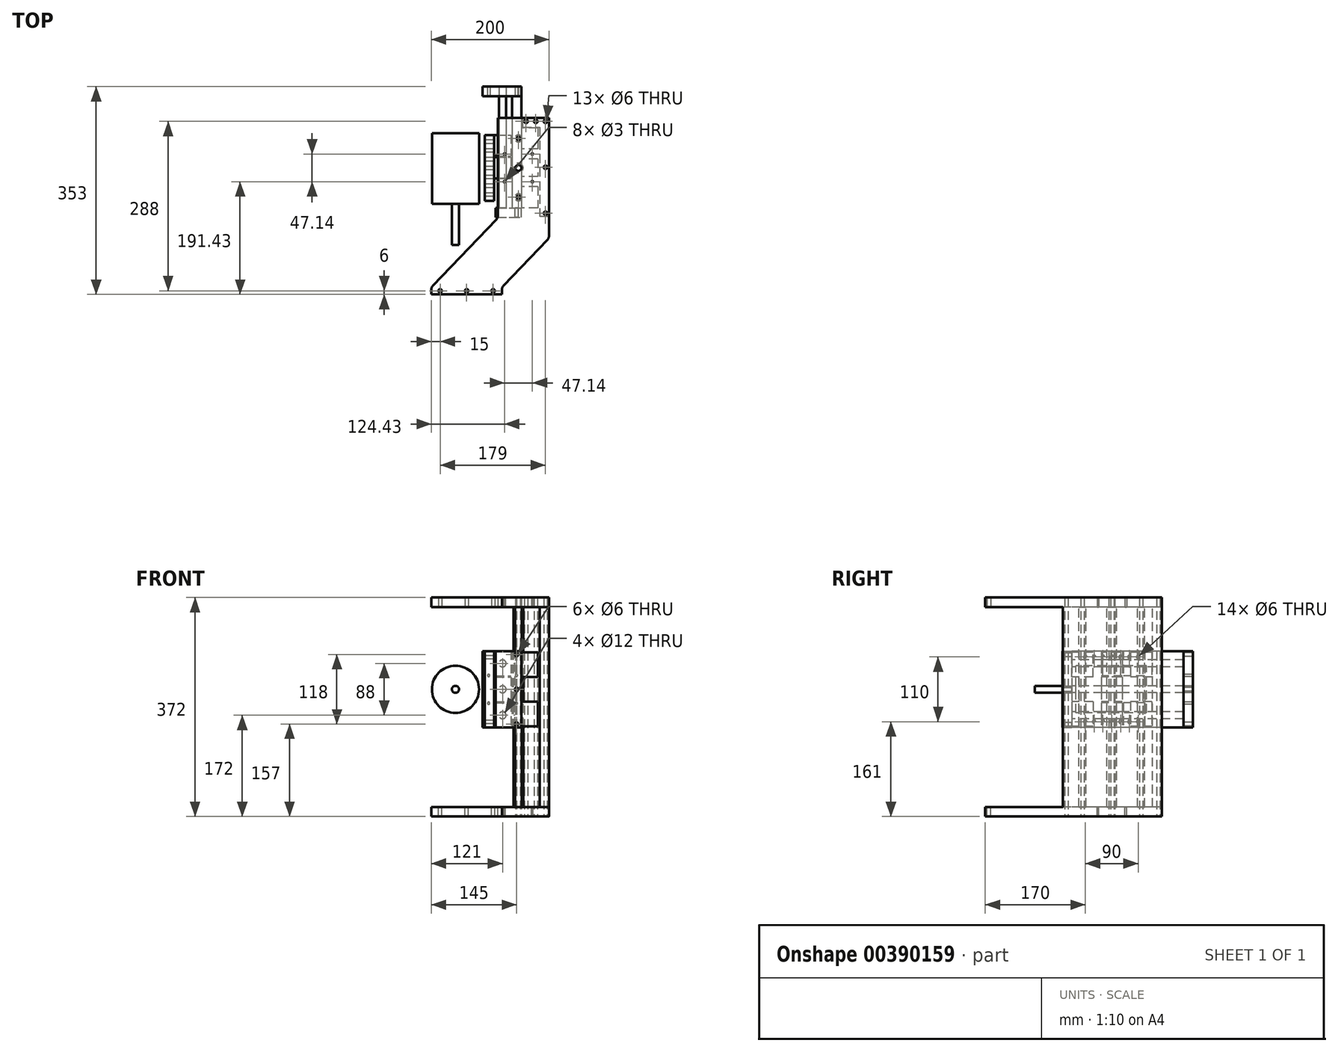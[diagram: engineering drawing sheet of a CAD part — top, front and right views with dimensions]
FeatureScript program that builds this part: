
annotation { "Feature Type Name" : "Feature", "Feature Type Description" : "" }
export const myFeature = defineFeature(function(context is Context, id is Id, definition is map)
    precondition{}
    {
        {
            var Q0;
            Q0=qCreatedBy(makeId("Top.planeOp"),FACE);
            var sketch = newSketch(context, id + "F0", { "sketchPlane" : qUnion([Q0])});
            skLineSegment(sketch, "E0", {"start": v(0, 0) * mm, "end": v(120, 0) * mm});
            skLineSegment(sketch, "E1", {"start": v(122.78, 14.9) * mm, "end": v(197.22, 92.64) * mm});
            skLineSegment(sketch, "E2", {"start": v(200, 99.56) * mm, "end": v(200, 300) * mm});
            skLineSegment(sketch, "E3", {"start": v(200, 300) * mm, "end": v(113, 300) * mm});
            skLineSegment(sketch, "E4", {"start": v(113, 300) * mm, "end": v(113, 134.02) * mm});
            skLineSegment(sketch, "E5", {"start": v(110.22, 127.1) * mm, "end": v(2.78, 14.9) * mm});
            skLineSegment(sketch, "E6.bottom", {"start": v(113, 300) * mm, "end": v(60, 300) * mm, "construction": true});
            skLineSegment(sketch, "E6.top", {"start": v(113, 240) * mm, "end": v(60, 240) * mm, "construction": true});
            skLineSegment(sketch, "E6.left", {"start": v(113, 300) * mm, "end": v(113, 240) * mm, "construction": true});
            skLineSegment(sketch, "E6.right", {"start": v(60, 300) * mm, "end": v(60, 240) * mm, "construction": true});
            skPoint(sketch, "E7", {"position": v(60, 0) * mm});
            skLineSegment(sketch, "E8", {"start": v(0, 0) * mm, "end": v(0, 7.98) * mm});
            skLineSegment(sketch, "E9", {"start": v(120, 0) * mm, "end": v(120, 7.98) * mm});
            skCircle(sketch, "E10", {"center": v(15, 6) * mm, "radius": 3 * mm});
            skCircle(sketch, "E11", {"center": v(105, 6) * mm, "radius": 3 * mm});
            skCircle(sketch, "E12", {"center": v(148, 165) * mm, "radius": 3 * mm});
            skCircle(sketch, "E13", {"center": v(148, 265) * mm, "radius": 3 * mm});
            skPoint(sketch, "E14", {"position": v(128, 300) * mm});
            skCircle(sketch, "E15", {"center": v(148, 215) * mm, "radius": 5 * mm});
            skLineSegment(sketch, "E16", {"start": v(148, 265) * mm, "end": v(148, 165) * mm, "construction": true});
            skCircle(sketch, "E17", {"center": v(194, 294) * mm, "radius": 3 * mm});
            skCircle(sketch, "E18", {"center": v(194, 216) * mm, "radius": 3 * mm});
            skCircle(sketch, "E19", {"center": v(194, 138) * mm, "radius": 3 * mm});
            skLineSegment(sketch, "E20", {"start": v(194, 138) * mm, "end": v(194, 294) * mm, "construction": true});
            skCircle(sketch, "E21", {"center": v(161, 294) * mm, "radius": 3 * mm});
            skPoint(sketch, "E22.visualSharp", {"position": v(0, 12) * mm});
            skArc(sketch, "E22.filletArc", {"start": v(2.78, 14.9) * mm, "mid": v(0.72, 11.71) * mm, "end": v(0, 7.98) * mm});
            skPoint(sketch, "E23.visualSharp", {"position": v(113, 130) * mm});
            skArc(sketch, "E23.filletArc", {"start": v(110.22, 127.1) * mm, "mid": v(112.28, 130.29) * mm, "end": v(113, 134.02) * mm});
            skArc(sketch, "E24.filletArc", {"start": v(197.22, 92.64) * mm, "mid": v(199.28, 95.83) * mm, "end": v(200, 99.56) * mm});
            skPoint(sketch, "E25.visualSharp", {"position": v(120, 12) * mm});
            skArc(sketch, "E25.filletArc", {"start": v(122.78, 14.9) * mm, "mid": v(120.72, 11.71) * mm, "end": v(120, 7.98) * mm});
            skCircle(sketch, "E26", {"center": v(60, 6) * mm, "radius": 3 * mm});
            skPoint(sketch, "E27", {"position": v(156.5, 300) * mm});
            skCircle(sketch, "E28", {"center": v(177.5, 294) * mm, "radius": 3 * mm});
            skCircle(sketch, "E29", {"center": v(148, 265) * mm, "radius": 6 * mm});
            skCircle(sketch, "E30", {"center": v(148, 165) * mm, "radius": 6 * mm});
            skCircle(sketch, "E31", {"center": v(148, 215) * mm, "radius": 8 * mm});
            skLineSegment(sketch, "E32.bottom", {"start": v(200, 300) * mm, "end": v(184, 300) * mm});
            skLineSegment(sketch, "E32.top", {"start": v(200, 132) * mm, "end": v(184, 132) * mm});
            skLineSegment(sketch, "E32.left", {"start": v(200, 300) * mm, "end": v(200, 132) * mm});
            skLineSegment(sketch, "E32.right", {"start": v(184, 300) * mm, "end": v(184, 132) * mm});
            skLineSegment(sketch, "E33.bottom", {"start": v(113, 300) * mm, "end": v(200, 300) * mm});
            skLineSegment(sketch, "E34", {"start": v(113, 284) * mm, "end": v(200, 284) * mm});
            skLineSegment(sketch, "E35", {"start": v(155, 300) * mm, "end": v(155, 284) * mm});
            skLineSegment(sketch, "E36", {"start": v(161, 294) * mm, "end": v(194, 294) * mm, "construction": true});
            skCircle(sketch, "E37", {"center": v(171.57, 238.57) * mm, "radius": 1.5 * mm});
            skCircle(sketch, "E38", {"center": v(124.43, 191.43) * mm, "radius": 1.5 * mm});
            skCircle(sketch, "E39", {"center": v(171.57, 191.43) * mm, "radius": 1.5 * mm});
            skLineSegment(sketch, "E40", {"start": v(171.57, 191.43) * mm, "end": v(171.57, 238.57) * mm, "construction": true});
            skLineSegment(sketch, "E41", {"start": v(124.43, 191.43) * mm, "end": v(171.57, 191.43) * mm, "construction": true});
            skPoint(sketch, "E42", {"position": v(171.57, 215) * mm});
            skPoint(sketch, "E43", {"position": v(148, 191.43) * mm});
            skCircle(sketch, "E44", {"center": v(124.43, 238.57) * mm, "radius": 1.5 * mm});
            skSolve(sketch);
        }
        {
            var Q0;
            Q0=makeQuery(id+"F0.imprint","IMPRINT",FACE,{"disambiguationData":[TD([[makeQuery(id+"F0.imprint","IMPRINT",EDGE,{"derivedFrom":sQuery(id+"F0.wireOp",EDGE,"E0")}),1.0]])]});
            var Q1;
            Q1=makeQuery(id+"F0.imprint","IMPRINT",FACE,{"disambiguationData":[TD([[makeQuery(id+"F0.imprint","IMPRINT",EDGE,{"derivedFrom":sQuery(id+"F0.wireOp",EDGE,"E13")}),-1.0]])]});
            var Q2;
            Q2=makeQuery(id+"F0.imprint","IMPRINT",FACE,{"disambiguationData":[TD([[makeQuery(id+"F0.imprint","IMPRINT",EDGE,{"derivedFrom":sQuery(id+"F0.wireOp",EDGE,"E15")}),-1.0]])]});
            var Q3;
            Q3=makeQuery(id+"F0.imprint","IMPRINT",FACE,{"disambiguationData":[TD([[makeQuery(id+"F0.imprint","IMPRINT",EDGE,{"derivedFrom":sQuery(id+"F0.wireOp",EDGE,"E12")}),-1.0]])]});
            var Q4;
            Q4=makeQuery(id+"F0.imprint","IMPRINT",FACE,{"disambiguationData":[TD([[makeQuery(id+"F0.imprint","IMPRINT",EDGE,{"derivedFrom":sQuery(id+"F0.wireOp",EDGE,"E17")}),-1.0]])]});
            var Q5;
            Q5=makeQuery(id+"F0.imprint","IMPRINT",FACE,{"disambiguationData":[TD([[makeQuery(id+"F0.imprint","IMPRINT",EDGE,{"derivedFrom":sQuery(id+"F0.wireOp",EDGE,"E21")}),-1.0]])]});
            var Q6;
            Q6=makeQuery(id+"F0.imprint","IMPRINT",FACE,{"disambiguationData":[TD([[makeQuery(id+"F0.imprint","IMPRINT",EDGE,{"derivedFrom":sQuery(id+"F0.wireOp",EDGE,"E18")}),-1.0]])]});
            var Q7;
            Q7=makeQuery(id+"F0.imprint","IMPRINT",FACE,{"disambiguationData":[TD([[makeQuery(id+"F0.imprint","IMPRINT",EDGE,{"derivedFrom":sQuery(id+"F0.wireOp",EDGE,"E28")}),-1.0]])]});
            var Q8;
            {var subQ5=sQuery(id+"F0.wireOp",EDGE,"E35");Q8=makeQuery(id+"F0.imprint","IMPRINT",FACE,{"disambiguationData":[TD([[makeQuery(id+"F0.imprint","IMPRINT",EDGE,{"derivedFrom":subQ5}),-1.0]])]});}
            extrude(context, id + "F1", {"entities" : qUnion([Q0, Q1, Q2, Q3, Q4, Q5, Q6, Q7, Q8]), "depth" : 16 * mm});
        }
        {
            var Q0;
            Q0=qCreatedBy(makeId("Top.planeOp"),FACE);
            cPlane(context, id + "F2", {"entities" : qUnion([Q0]), "cplaneType" : CPlaneType.OFFSET, "offset" : 170 * mm, "oppositeDirection" : true, "width" : 150 * mm, "height" : 150 * mm});
        }
        {
            var Q0;
            Q0=makeQuery(id+"F1.opExtrude","SWEPT_BODY",BODY,{"disambiguationData":[OSD([sQuery(id+"F0.wireOp",EDGE,"E0"),sQuery(id+"F0.wireOp",EDGE,"E1"),sQuery(id+"F0.wireOp",EDGE,"E2"),sQuery(id+"F0.wireOp",EDGE,"E3"),sQuery(id+"F0.wireOp",EDGE,"E4"),sQuery(id+"F0.wireOp",EDGE,"E5"),sQuery(id+"F0.wireOp",EDGE,"E8"),sQuery(id+"F0.wireOp",EDGE,"E9"),sQuery(id+"F0.wireOp",EDGE,"E10"),sQuery(id+"F0.wireOp",EDGE,"E11"),sQuery(id+"F0.wireOp",EDGE,"E12"),sQuery(id+"F0.wireOp",EDGE,"E13"),sQuery(id+"F0.wireOp",EDGE,"E15"),sQuery(id+"F0.wireOp",EDGE,"E17"),sQuery(id+"F0.wireOp",EDGE,"E18"),sQuery(id+"F0.wireOp",EDGE,"E19"),sQuery(id+"F0.wireOp",EDGE,"E21"),sQuery(id+"F0.wireOp",EDGE,"E22.filletArc"),sQuery(id+"F0.wireOp",EDGE,"E23.filletArc"),sQuery(id+"F0.wireOp",EDGE,"E24.filletArc"),sQuery(id+"F0.wireOp",EDGE,"E25.filletArc"),sQuery(id+"F0.wireOp",EDGE,"E26"),sQuery(id+"F0.wireOp",EDGE,"E28")])]});
            var Q1;
            Q1=qCreatedBy(id+"F2.planeOp",FACE);
            mirror(context, id + "F3", {"entities" : qUnion([Q0]), "mirrorPlane" : qUnion([Q1])});
        }
        {
            var Q0;
            Q0=makeQuery(id+"F0.imprint","IMPRINT",FACE,{"disambiguationData":[TD([[makeQuery(id+"F0.imprint","IMPRINT",EDGE,{"derivedFrom":sQuery(id+"F0.wireOp",EDGE,"E13")}),-1.0]])]});
            var Q1;
            Q1=makeQuery(id+"F0.imprint","IMPRINT",FACE,{"disambiguationData":[TD([[makeQuery(id+"F0.imprint","IMPRINT",EDGE,{"derivedFrom":sQuery(id+"F0.wireOp",EDGE,"E12")}),-1.0]])]});
            var Q2;
            Q2=makeQuery(id+"F0.imprint","IMPRINT",FACE,{"disambiguationData":[TD([[makeQuery(id+"F0.imprint","IMPRINT",EDGE,{"derivedFrom":sQuery(id+"F0.wireOp",EDGE,"E15")}),-1.0]])]});
            var Q3;
            Q3=qCreatedBy(id+"F2.planeOp",FACE);
            extrude(context, id + "F4", {"entities" : qUnion([Q0, Q1, Q2]), "endBound" : BoundingType.UP_TO_SURFACE, "oppositeDirection" : true, "endBoundEntityFace" : qUnion([Q3]), "depth" : 100 * mm});
        }
        {
            var Q0;
            Q0=makeQuery(id+"F4.opExtrude","SWEPT_BODY",BODY,{"disambiguationData":[OSD([sQuery(id+"F0.wireOp",EDGE,"E12"),sQuery(id+"F0.wireOp",EDGE,"E30")])]});
            var Q1;
            Q1=makeQuery(id+"F4.opExtrude","SWEPT_BODY",BODY,{"disambiguationData":[OSD([sQuery(id+"F0.wireOp",EDGE,"E15"),sQuery(id+"F0.wireOp",EDGE,"E31")])]});
            var Q2;
            Q2=makeQuery(id+"F4.opExtrude","SWEPT_BODY",BODY,{"disambiguationData":[OSD([sQuery(id+"F0.wireOp",EDGE,"E13"),sQuery(id+"F0.wireOp",EDGE,"E29")])]});
            var Q3;
            Q3=qCreatedBy(id+"F2.planeOp",FACE);
            mirror(context, id + "F5", {"operationType" : NewBodyOperationType.ADD, "entities" : qUnion([Q0, Q1, Q2]), "mirrorPlane" : qUnion([Q3])});
        }
        {
            var Q0;
            Q0=makeQuery(id+"F1.opExtrude","SWEPT_FACE",FACE,{"disambiguationData":[OSD([sQuery(id+"F0.wireOp",EDGE,"E4")])]});
            cPlane(context, id + "F6", {"entities" : qUnion([Q0]), "cplaneType" : CPlaneType.OFFSET, "offset" : 40 * mm, "oppositeDirection" : true, "width" : 150 * mm, "height" : 150 * mm});
        }
        {
            var Q0;
            Q0=qCreatedBy(id+"F6.planeOp",FACE);
            var sketch = newSketch(context, id + "F7", { "sketchPlane" : qUnion([Q0])});
            skLineSegment(sketch, "E45.bottom", {"start": v(-283, -77) * mm, "end": v(-247, -77) * mm});
            skLineSegment(sketch, "E45.top", {"start": v(-283, -119) * mm, "end": v(-247, -119) * mm});
            skLineSegment(sketch, "E45.left", {"start": v(-283, -77) * mm, "end": v(-283, -119) * mm});
            skLineSegment(sketch, "E45.right", {"start": v(-247, -77) * mm, "end": v(-247, -119) * mm});
            skPoint(sketch, "E46", {"position": v(-265, -77) * mm});
            skLineSegment(sketch, "E47.bottom", {"start": v(-183, -119) * mm, "end": v(-147, -119) * mm});
            skLineSegment(sketch, "E47.top", {"start": v(-183, -77) * mm, "end": v(-147, -77) * mm});
            skLineSegment(sketch, "E47.left", {"start": v(-183, -119) * mm, "end": v(-183, -77) * mm});
            skLineSegment(sketch, "E47.right", {"start": v(-147, -119) * mm, "end": v(-147, -77) * mm});
            skPoint(sketch, "E48", {"position": v(-165, -77) * mm});
            skLineSegment(sketch, "E49.bottom", {"start": v(-230, -119) * mm, "end": v(-200, -119) * mm});
            skLineSegment(sketch, "E49.top", {"start": v(-230, -77) * mm, "end": v(-200, -77) * mm});
            skLineSegment(sketch, "E49.left", {"start": v(-230, -119) * mm, "end": v(-230, -77) * mm});
            skLineSegment(sketch, "E49.right", {"start": v(-200, -119) * mm, "end": v(-200, -77) * mm});
            skPoint(sketch, "E50", {"position": v(-215, -77) * mm});
            skLineSegment(sketch, "E51.bottom", {"start": v(-337, -75) * mm, "end": v(-147, -75) * mm});
            skLineSegment(sketch, "E51.top", {"start": v(-337, -205) * mm, "end": v(-147, -205) * mm});
            skLineSegment(sketch, "E51.left", {"start": v(-337, -75) * mm, "end": v(-337, -205) * mm});
            skLineSegment(sketch, "E51.right", {"start": v(-147, -75) * mm, "end": v(-147, -205) * mm});
            skPoint(sketch, "E52", {"position": v(-200, -98) * mm});
            skPoint(sketch, "E53.oppositeSnap0", {"position": v(-247, -98) * mm});
            skLineSegment(sketch, "E53.bottom", {"start": v(-283, -161) * mm, "end": v(-247, -161) * mm});
            skLineSegment(sketch, "E53.top", {"start": v(-283, -203) * mm, "end": v(-247, -203) * mm});
            skLineSegment(sketch, "E53.left", {"start": v(-283, -161) * mm, "end": v(-283, -203) * mm});
            skLineSegment(sketch, "E53.right", {"start": v(-247, -161) * mm, "end": v(-247, -203) * mm});
            skPoint(sketch, "E54.firstSnap0", {"position": v(-230, -98) * mm});
            skPoint(sketch, "E55.firstSnap0", {"position": v(-183, -98) * mm});
            skLineSegment(sketch, "E55.bottom", {"start": v(-183, -161) * mm, "end": v(-147, -161) * mm});
            skLineSegment(sketch, "E55.top", {"start": v(-183, -203) * mm, "end": v(-147, -203) * mm});
            skLineSegment(sketch, "E55.left", {"start": v(-183, -161) * mm, "end": v(-183, -203) * mm});
            skLineSegment(sketch, "E55.right", {"start": v(-147, -161) * mm, "end": v(-147, -203) * mm});
            skLineSegment(sketch, "E56.0", {"start": v(-300, 0) * mm, "end": v(-134.02, 0) * mm, "construction": true});
            skSolve(sketch);
        }
        {
            var Q0;
            Q0=makeQuery(id+"F7.imprint","IMPRINT",FACE,{"disambiguationData":[TD([[makeQuery(id+"F7.imprint","IMPRINT",EDGE,{"derivedFrom":sQuery(id+"F7.wireOp",EDGE,"E45.bottom")}),-1.0]])]});
            var Q1;
            Q1=makeQuery(id+"F7.imprint","IMPRINT",FACE,{"disambiguationData":[TD([[makeQuery(id+"F7.imprint","IMPRINT",EDGE,{"derivedFrom":sQuery(id+"F7.wireOp",EDGE,"E47.bottom")}),1.0]])]});
            var Q2;
            Q2=makeQuery(id+"F7.imprint","IMPRINT",FACE,{"disambiguationData":[TD([[makeQuery(id+"F7.imprint","IMPRINT",EDGE,{"derivedFrom":sQuery(id+"F7.wireOp",EDGE,"E49.bottom")}),1.0]])]});
            var Q3;
            Q3=makeQuery(id+"F7.imprint","IMPRINT",FACE,{"disambiguationData":[TD([[makeQuery(id+"F7.imprint","IMPRINT",EDGE,{"derivedFrom":sQuery(id+"F7.wireOp",EDGE,"E53.bottom")}),-1.0]])]});
            var Q4;
            Q4=makeQuery(id+"F7.imprint","IMPRINT",FACE,{"disambiguationData":[TD([[makeQuery(id+"F7.imprint","IMPRINT",EDGE,{"derivedFrom":sQuery(id+"F7.wireOp",EDGE,"E54.bottom")}),-1.0]])]});
            var Q5;
            Q5=makeQuery(id+"F7.imprint","IMPRINT",FACE,{"disambiguationData":[TD([[makeQuery(id+"F7.imprint","IMPRINT",EDGE,{"derivedFrom":sQuery(id+"F7.wireOp",EDGE,"E55.bottom")}),-1.0]])]});
            extrude(context, id + "F8", {"entities" : qUnion([Q0, Q1, Q2, Q3, Q4, Q5]), "oppositeDirection" : true, "depth" : 28 * mm});
        }
        {
            var Q0;
            Q0=makeQuery(id+"F7.imprint","IMPRINT",FACE,{"disambiguationData":[TD([[makeQuery(id+"F7.imprint","IMPRINT",EDGE,{"derivedFrom":sQuery(id+"F7.wireOp",EDGE,"E45.bottom")}),1.0]])]});
            var Q1;
            Q1=makeQuery(id+"F7.imprint","IMPRINT",FACE,{"disambiguationData":[TD([[makeQuery(id+"F7.imprint","IMPRINT",EDGE,{"derivedFrom":sQuery(id+"F7.wireOp",EDGE,"E47.bottom")}),1.0]])]});
            var Q2;
            Q2=makeQuery(id+"F7.imprint","IMPRINT",FACE,{"disambiguationData":[TD([[makeQuery(id+"F7.imprint","IMPRINT",EDGE,{"derivedFrom":sQuery(id+"F7.wireOp",EDGE,"E49.bottom")}),1.0]])]});
            var Q3;
            Q3=makeQuery(id+"F7.imprint","IMPRINT",FACE,{"disambiguationData":[TD([[makeQuery(id+"F7.imprint","IMPRINT",EDGE,{"derivedFrom":sQuery(id+"F7.wireOp",EDGE,"E45.bottom")}),-1.0]])]});
            var Q4;
            Q4=makeQuery(id+"F7.imprint","IMPRINT",FACE,{"disambiguationData":[TD([[makeQuery(id+"F7.imprint","IMPRINT",EDGE,{"derivedFrom":sQuery(id+"F7.wireOp",EDGE,"E53.bottom")}),-1.0]])]});
            var Q5;
            Q5=makeQuery(id+"F7.imprint","IMPRINT",FACE,{"disambiguationData":[TD([[makeQuery(id+"F7.imprint","IMPRINT",EDGE,{"derivedFrom":sQuery(id+"F7.wireOp",EDGE,"E54.bottom")}),-1.0]])]});
            var Q6;
            Q6=makeQuery(id+"F7.imprint","IMPRINT",FACE,{"disambiguationData":[TD([[makeQuery(id+"F7.imprint","IMPRINT",EDGE,{"derivedFrom":sQuery(id+"F7.wireOp",EDGE,"E55.bottom")}),-1.0]])]});
            extrude(context, id + "F9", {"entities" : qUnion([Q0, Q1, Q2, Q3, Q4, Q5, Q6]), "depth" : 16 * mm});
        }
        {
            var Q0;
            Q0=makeQuery(id+"F9.opExtrude","SWEPT_FACE",FACE,{"disambiguationData":[OSD([sQuery(id+"F7.wireOp",EDGE,"E51.left")])]});
            cPlane(context, id + "F10", {"entities" : qUnion([Q0]), "cplaneType" : CPlaneType.OFFSET, "offset" : 0 * mm, "width" : 150 * mm, "height" : 150 * mm});
        }
        {
            var Q0;
            Q0=qCreatedBy(id+"F10.planeOp",FACE);
            var sketch = newSketch(context, id + "F11", { "sketchPlane" : qUnion([Q0])});
            skLineSegment(sketch, "E57.top", {"start": v(-153, -205) * mm, "end": v(-87, -205) * mm});
            skLineSegment(sketch, "E57.left", {"start": v(-153, -75) * mm, "end": v(-153, -205) * mm});
            skLineSegment(sketch, "E57.right", {"start": v(-87, -75) * mm, "end": v(-87, -205) * mm});
            skLineSegment(sketch, "E58", {"start": v(-137, -75) * mm, "end": v(-137, -205) * mm});
            skPoint(sketch, "E59", {"position": v(-112, -75) * mm});
            skPoint(sketch, "E60", {"position": v(-87, -140) * mm});
            skLineSegment(sketch, "E61", {"start": v(-153, -75) * mm, "end": v(-137, -75) * mm});
            skLineSegment(sketch, "E62", {"start": v(-87, -75) * mm, "end": v(-137, -75) * mm});
            skCircle(sketch, "E63", {"center": v(-145, -81) * mm, "radius": 3 * mm});
            skCircle(sketch, "E64", {"center": v(-145, -140) * mm, "radius": 3 * mm});
            skCircle(sketch, "E65", {"center": v(-145, -199) * mm, "radius": 3 * mm});
            skLineSegment(sketch, "E66", {"start": v(-145, -199) * mm, "end": v(-145, -81) * mm, "construction": true});
            skPoint(sketch, "E67", {"position": v(-145, -75) * mm});
            skPoint(sketch, "E68", {"position": v(-137, -140) * mm});
            skLineSegment(sketch, "E69.0", {"start": v(-137, -205) * mm, "end": v(-153, -205) * mm, "construction": true});
            skLineSegment(sketch, "E70.0", {"start": v(-137, -75) * mm, "end": v(-153, -75) * mm, "construction": true});
            skCircle(sketch, "E71", {"center": v(-121, -140) * mm, "radius": 6 * mm});
            skCircle(sketch, "E72", {"center": v(-144.57, -116.43) * mm, "radius": 2 * mm});
            skCircle(sketch, "E73", {"center": v(-97.43, -116.43) * mm, "radius": 2 * mm});
            skCircle(sketch, "E74", {"center": v(-97.43, -163.57) * mm, "radius": 2 * mm});
            skCircle(sketch, "E75", {"center": v(-144.57, -163.57) * mm, "radius": 2 * mm});
            skLineSegment(sketch, "E76", {"start": v(-144.57, -163.57) * mm, "end": v(-97.43, -163.57) * mm, "construction": true});
            skLineSegment(sketch, "E77", {"start": v(-97.43, -163.57) * mm, "end": v(-97.43, -116.43) * mm, "construction": true});
            skPoint(sketch, "E78", {"position": v(-121, -163.57) * mm});
            skPoint(sketch, "E79", {"position": v(-97.43, -140) * mm});
            skSolve(sketch);
        }
        {
            var Q0;
            {var subQ0=sQuery(id+"F11.wireOp",EDGE,"E57.right");Q0=makeQuery(id+"F11.imprint","IMPRINT",FACE,{"disambiguationData":[TD([[makeQuery(id+"F11.imprint","IMPRINT",EDGE,{"derivedFrom":subQ0}),-1.0]])]});}
            var Q1;
            {var subQ1=sQuery(id+"F11.wireOp",EDGE,"E57.left");Q1=makeQuery(id+"F11.imprint","IMPRINT",FACE,{"disambiguationData":[TD([[makeQuery(id+"F11.imprint","IMPRINT",EDGE,{"derivedFrom":subQ1}),1.0]])]});}
            extrude(context, id + "F12", {"entities" : qUnion([Q0, Q1]), "depth" : 16 * mm});
        }
        {
            var Q0;
            Q0=makeQuery(id+"F9.opExtrude","SWEPT_FACE",FACE,{"disambiguationData":[OSD([sQuery(id+"F7.wireOp",EDGE,"E51.right")])]});
            cPlane(context, id + "F13", {"entities" : qUnion([Q0]), "cplaneType" : CPlaneType.OFFSET, "offset" : 0 * mm, "width" : 150 * mm, "height" : 150 * mm});
        }
        {
            var Q0;
            Q0=qCreatedBy(id+"F13.planeOp",FACE);
            var sketch = newSketch(context, id + "F14", { "sketchPlane" : qUnion([Q0])});
            skLineSegment(sketch, "E80.bottom", {"start": v(109, -75) * mm, "end": v(153, -75) * mm});
            skLineSegment(sketch, "E80.top", {"start": v(109, -205) * mm, "end": v(153, -205) * mm});
            skLineSegment(sketch, "E80.left", {"start": v(109, -75) * mm, "end": v(109, -205) * mm});
            skLineSegment(sketch, "E80.right", {"start": v(153, -75) * mm, "end": v(153, -205) * mm});
            skLineSegment(sketch, "E81", {"start": v(137, -75) * mm, "end": v(137, -205) * mm, "construction": true});
            skCircle(sketch, "E82.0", {"center": v(145, -81) * mm, "radius": 3 * mm});
            skCircle(sketch, "E82.1", {"center": v(145, -199) * mm, "radius": 3 * mm});
            skCircle(sketch, "E82.2", {"center": v(145, -140) * mm, "radius": 3 * mm});
            skLineSegment(sketch, "E83.0", {"start": v(87, -75) * mm, "end": v(153, -75) * mm, "construction": true});
            skSolve(sketch);
        }
        {
            var Q0;
            Q0=makeQuery(id+"F14.imprint","IMPRINT",FACE,{"disambiguationData":[TD([[makeQuery(id+"F14.imprint","IMPRINT",EDGE,{"derivedFrom":sQuery(id+"F14.wireOp",EDGE,"E80.bottom")}),-1.0]])]});
            extrude(context, id + "F15", {"entities" : qUnion([Q0]), "depth" : 16 * mm});
        }
        {
            var Q0;
            Q0=makeQuery(id+"F0.imprint","IMPRINT",FACE,{"disambiguationData":[TD([[makeQuery(id+"F0.imprint","IMPRINT",EDGE,{"derivedFrom":sQuery(id+"F0.wireOp",EDGE,"E18")}),-1.0]])]});
            var Q1;
            Q1=qCreatedBy(id+"F2.planeOp",FACE);
            extrude(context, id + "F16", {"entities" : qUnion([Q0]), "endBound" : BoundingType.UP_TO_SURFACE, "oppositeDirection" : true, "endBoundEntityFace" : qUnion([Q1]), "depth" : 100 * mm});
        }
        {
            var Q0;
            Q0=makeQuery(id+"F16.opExtrude","SWEPT_BODY",BODY,{"disambiguationData":[OSD([sQuery(id+"F0.wireOp",EDGE,"E17"),sQuery(id+"F0.wireOp",EDGE,"E18"),sQuery(id+"F0.wireOp",EDGE,"E19"),sQuery(id+"F0.wireOp",EDGE,"E24.filletArc"),sQuery(id+"F0.wireOp",EDGE,"E32.bottom"),sQuery(id+"F0.wireOp",EDGE,"E32.top"),sQuery(id+"F0.wireOp",EDGE,"E32.left"),sQuery(id+"F0.wireOp",EDGE,"E32.right")])]});
            var Q1;
            Q1=qCreatedBy(id+"F2.planeOp",FACE);
            mirror(context, id + "F17", {"operationType" : NewBodyOperationType.ADD, "entities" : qUnion([Q0]), "mirrorPlane" : qUnion([Q1])});
        }
        {
            var Q0;
            Q0=makeQuery(id+"F0.imprint","IMPRINT",FACE,{"disambiguationData":[TD([[makeQuery(id+"F0.imprint","IMPRINT",EDGE,{"derivedFrom":sQuery(id+"F0.wireOp",EDGE,"E28")}),-1.0]])]});
            var Q1;
            Q1=makeQuery(id+"F0.imprint","IMPRINT",FACE,{"disambiguationData":[TD([[makeQuery(id+"F0.imprint","IMPRINT",EDGE,{"derivedFrom":sQuery(id+"F0.wireOp",EDGE,"E17")}),-1.0]])]});
            var Q2;
            Q2=qCreatedBy(id+"F2.planeOp",FACE);
            extrude(context, id + "F18", {"entities" : qUnion([Q0, Q1]), "endBound" : BoundingType.UP_TO_SURFACE, "oppositeDirection" : true, "endBoundEntityFace" : qUnion([Q2]), "depth" : 100 * mm});
        }
        {
            var Q0;
            Q0=makeQuery(id+"F18.opExtrude","SWEPT_BODY",BODY,{"disambiguationData":[OSD([sQuery(id+"F0.wireOp",EDGE,"E4"),sQuery(id+"F0.wireOp",EDGE,"E32.right"),sQuery(id+"F0.wireOp",EDGE,"E33.bottom"),sQuery(id+"F0.wireOp",EDGE,"E34")])]});
            var Q1;
            Q1=qCreatedBy(id+"F2.planeOp",FACE);
            mirror(context, id + "F19", {"operationType" : NewBodyOperationType.ADD, "entities" : qUnion([Q0]), "mirrorPlane" : qUnion([Q1])});
        }
        {
            var Q0;
            Q0=makeQuery(id+"F15.opExtrude","CAP_FACE",FACE,{"disambiguationData":[OSD([sQuery(id+"F14.wireOp",EDGE,"E80.bottom"),sQuery(id+"F14.wireOp",EDGE,"E80.top"),sQuery(id+"F14.wireOp",EDGE,"E80.left"),sQuery(id+"F14.wireOp",EDGE,"E80.right")])],"isStart":true});
            cPlane(context, id + "F20", {"entities" : qUnion([Q0]), "cplaneType" : CPlaneType.OFFSET, "offset" : 0 * mm, "width" : 150 * mm, "height" : 150 * mm});
        }
        {
            var Q0;
            Q0=qCreatedBy(id+"F20.planeOp",FACE);
            var sketch = newSketch(context, id + "F21", { "sketchPlane" : qUnion([Q0])});
            skCircle(sketch, "E84", {"center": v(-121, -96) * mm, "radius": 6 * mm});
            skCircle(sketch, "E85", {"center": v(-121, -184) * mm, "radius": 6 * mm});
            skCircle(sketch, "E86", {"center": v(-121, -140) * mm, "radius": 6 * mm});
            skLineSegment(sketch, "E87", {"start": v(-121, -96) * mm, "end": v(-121, -184) * mm, "construction": true});
            skLineSegment(sketch, "E88.0", {"start": v(-109, -75) * mm, "end": v(-109, -205) * mm, "construction": true});
            skSolve(sketch);
        }
        {
            var Q0;
            Q0=makeQuery(id+"F21.imprint","IMPRINT",FACE,{"disambiguationData":[TD([[makeQuery(id+"F21.imprint","IMPRINT",EDGE,{"derivedFrom":sQuery(id+"F21.wireOp",EDGE,"E85")}),1.0]])]});
            var Q1;
            Q1=makeQuery(id+"F21.imprint","IMPRINT",FACE,{"disambiguationData":[TD([[makeQuery(id+"F21.imprint","IMPRINT",EDGE,{"derivedFrom":sQuery(id+"F21.wireOp",EDGE,"E86")}),1.0]])]});
            var Q2;
            Q2=makeQuery(id+"F21.imprint","IMPRINT",FACE,{"disambiguationData":[TD([[makeQuery(id+"F21.imprint","IMPRINT",EDGE,{"derivedFrom":sQuery(id+"F21.wireOp",EDGE,"E84")}),1.0]])]});
            extrude(context, id + "F22", {"entities" : qUnion([Q0, Q1, Q2]), "depth" : 190 * mm});
        }
        {
            var Q0;
            Q0=qCreatedBy(id+"F20.planeOp",FACE);
            cPlane(context, id + "F23", {"entities" : qUnion([Q0]), "cplaneType" : CPlaneType.OFFSET, "offset" : 50 * mm, "width" : 150 * mm, "height" : 150 * mm});
        }
        {
            var Q0;
            Q0=qCreatedBy(id+"F23.planeOp",FACE);
            var sketch = newSketch(context, id + "F24", { "sketchPlane" : qUnion([Q0])});
            skCircle(sketch, "E89.0", {"center": v(-121, -96) * mm, "radius": 6 * mm});
            skCircle(sketch, "E89.1", {"center": v(-121, -140) * mm, "radius": 6 * mm});
            skCircle(sketch, "E89.2", {"center": v(-121, -184) * mm, "radius": 6 * mm});
            skLineSegment(sketch, "E90.bottom", {"start": v(-107, -75) * mm, "end": v(-135, -75) * mm});
            skLineSegment(sketch, "E90.top", {"start": v(-107, -117) * mm, "end": v(-135, -117) * mm});
            skLineSegment(sketch, "E90.left", {"start": v(-107, -75) * mm, "end": v(-107, -117) * mm});
            skLineSegment(sketch, "E90.right", {"start": v(-135, -75) * mm, "end": v(-135, -117) * mm});
            skLineSegment(sketch, "E91.bottom", {"start": v(-107, -163) * mm, "end": v(-135, -163) * mm});
            skLineSegment(sketch, "E91.top", {"start": v(-107, -205) * mm, "end": v(-135, -205) * mm});
            skLineSegment(sketch, "E91.left", {"start": v(-107, -163) * mm, "end": v(-107, -205) * mm});
            skLineSegment(sketch, "E91.right", {"start": v(-135, -163) * mm, "end": v(-135, -205) * mm});
            skLineSegment(sketch, "E92.bottom", {"start": v(-107, -119) * mm, "end": v(-135, -119) * mm});
            skLineSegment(sketch, "E92.top", {"start": v(-107, -161) * mm, "end": v(-135, -161) * mm});
            skLineSegment(sketch, "E92.left", {"start": v(-107, -119) * mm, "end": v(-107, -161) * mm});
            skLineSegment(sketch, "E92.right", {"start": v(-135, -119) * mm, "end": v(-135, -161) * mm});
            skSolve(sketch);
        }
        {
            var Q0;
            Q0=makeQuery(id+"F24.imprint","IMPRINT",FACE,{"disambiguationData":[TD([[makeQuery(id+"F24.imprint","IMPRINT",EDGE,{"derivedFrom":sQuery(id+"F24.wireOp",EDGE,"E89.2")}),-1.0]])]});
            var Q1;
            Q1=makeQuery(id+"F24.imprint","IMPRINT",FACE,{"disambiguationData":[TD([[makeQuery(id+"F24.imprint","IMPRINT",EDGE,{"derivedFrom":sQuery(id+"F24.wireOp",EDGE,"E89.0")}),-1.0]])]});
            extrude(context, id + "F25", {"entities" : qUnion([Q0, Q1]), "depth" : 36 * mm});
        }
        {
            var Q0;
            Q0=makeQuery(id+"F24.imprint","IMPRINT",FACE,{"disambiguationData":[TD([[makeQuery(id+"F24.imprint","IMPRINT",EDGE,{"derivedFrom":sQuery(id+"F24.wireOp",EDGE,"E89.1")}),-1.0]])]});
            extrude(context, id + "F26", {"entities" : qUnion([Q0]), "depth" : 36 * mm});
        }
        {
            var Q0;
            Q0=makeQuery(id+"F25.opExtrude","SWEPT_FACE",FACE,{"disambiguationData":[OSD([sQuery(id+"F24.wireOp",EDGE,"E90.left")])]});
            cPlane(context, id + "F27", {"entities" : qUnion([Q0]), "cplaneType" : CPlaneType.OFFSET, "offset" : 0 * mm, "width" : 150 * mm, "height" : 150 * mm});
        }
        {
            var Q0;
            Q0=qCreatedBy(id+"F27.planeOp",FACE);
            var sketch = newSketch(context, id + "F28", { "sketchPlane" : qUnion([Q0])});
            skLineSegment(sketch, "E93.bottom", {"start": v(-271, -75) * mm, "end": v(-159, -75) * mm});
            skLineSegment(sketch, "E93.top", {"start": v(-271, -205) * mm, "end": v(-159, -205) * mm});
            skLineSegment(sketch, "E93.left", {"start": v(-271, -75) * mm, "end": v(-271, -205) * mm});
            skLineSegment(sketch, "E93.right", {"start": v(-159, -75) * mm, "end": v(-159, -205) * mm});
            skLineSegment(sketch, "E94.0", {"start": v(-233, -75) * mm, "end": v(-197, -75) * mm, "construction": true});
            skPoint(sketch, "E95", {"position": v(-215, -75) * mm});
            skPoint(sketch, "E96", {"position": v(-159, -140) * mm});
            skLineSegment(sketch, "E97.0", {"start": v(-197, -119) * mm, "end": v(-197, -161) * mm, "construction": true});
            skPoint(sketch, "E98", {"position": v(-197, -140) * mm});
            skCircle(sketch, "E99", {"center": v(-215, -85) * mm, "radius": 3 * mm});
            skCircle(sketch, "E100", {"center": v(-215, -195) * mm, "radius": 3 * mm});
            skLineSegment(sketch, "E101", {"start": v(-215, -75) * mm, "end": v(-215, -205) * mm, "construction": true});
            skPoint(sketch, "E102", {"position": v(-215, -140) * mm});
            skCircle(sketch, "E103", {"center": v(-200, -85) * mm, "radius": 3 * mm});
            skCircle(sketch, "E104", {"center": v(-185, -85) * mm, "radius": 3 * mm});
            skCircle(sketch, "E105", {"center": v(-170, -85) * mm, "radius": 3 * mm});
            skCircle(sketch, "E106", {"center": v(-230, -85) * mm, "radius": 3 * mm});
            skCircle(sketch, "E107", {"center": v(-245, -85) * mm, "radius": 3 * mm});
            skCircle(sketch, "E108", {"center": v(-260, -85) * mm, "radius": 3 * mm});
            skCircle(sketch, "E109", {"center": v(-185, -195) * mm, "radius": 3 * mm});
            skCircle(sketch, "E110", {"center": v(-170, -195) * mm, "radius": 3 * mm});
            skCircle(sketch, "E111", {"center": v(-230, -195) * mm, "radius": 3 * mm});
            skCircle(sketch, "E112", {"center": v(-245, -195) * mm, "radius": 3 * mm});
            skCircle(sketch, "E113", {"center": v(-260, -195) * mm, "radius": 3 * mm});
            skCircle(sketch, "E114", {"center": v(-200, -195) * mm, "radius": 3 * mm});
            skSolve(sketch);
        }
        {
            var Q0;
            Q0=makeQuery(id+"F28.imprint","IMPRINT",FACE,{"disambiguationData":[TD([[makeQuery(id+"F28.imprint","IMPRINT",EDGE,{"derivedFrom":sQuery(id+"F28.wireOp",EDGE,"E93.bottom")}),-1.0]])]});
            extrude(context, id + "F29", {"entities" : qUnion([Q0]), "depth" : 16 * mm});
        }
        {
            var Q0;
            Q0=makeQuery(id+"F29.opExtrude","SWEPT_FACE",FACE,{"disambiguationData":[OSD([sQuery(id+"F28.wireOp",EDGE,"E93.right")])]});
            cPlane(context, id + "F30", {"entities" : qUnion([Q0]), "cplaneType" : CPlaneType.OFFSET, "offset" : 5 * mm, "width" : 150 * mm, "height" : 150 * mm});
        }
        {
            var Q0;
            Q0=qCreatedBy(id+"F30.planeOp",FACE);
            var sketch = newSketch(context, id + "F31", { "sketchPlane" : qUnion([Q0])});
            skLineSegment(sketch, "E115.0", {"start": v(91, -75) * mm, "end": v(91, -205) * mm, "construction": true});
            skPoint(sketch, "E116", {"position": v(91, -140) * mm});
            skCircle(sketch, "E117", {"center": v(41, -140) * mm, "radius": 40 * mm});
            skCircle(sketch, "E118", {"center": v(41, -140) * mm, "radius": 6 * mm});
            skSolve(sketch);
        }
        {
            var Q0;
            Q0=makeQuery(id+"F31.imprint","IMPRINT",FACE,{"disambiguationData":[TD([[makeQuery(id+"F31.imprint","IMPRINT",EDGE,{"derivedFrom":sQuery(id+"F31.wireOp",EDGE,"E117")}),1.0]])]});
            var Q1;
            Q1=makeQuery(id+"F31.imprint","IMPRINT",FACE,{"disambiguationData":[TD([[makeQuery(id+"F31.imprint","IMPRINT",EDGE,{"derivedFrom":sQuery(id+"F31.wireOp",EDGE,"E118")}),1.0]])]});
            extrude(context, id + "F32", {"entities" : qUnion([Q0, Q1]), "oppositeDirection" : true, "depth" : 120 * mm});
        }
        {
            var Q0;
            Q0=makeQuery(id+"F31.imprint","IMPRINT",FACE,{"disambiguationData":[TD([[makeQuery(id+"F31.imprint","IMPRINT",EDGE,{"derivedFrom":sQuery(id+"F31.wireOp",EDGE,"E118")}),1.0]])]});
            extrude(context, id + "F33", {"entities" : qUnion([Q0]), "operationType" : NewBodyOperationType.ADD, "depth" : 70 * mm});
        }
        {
            var Q0;
            Q0=qCreatedBy(id+"F23.planeOp",FACE);
            cPlane(context, id + "F34", {"entities" : qUnion([Q0]), "cplaneType" : CPlaneType.OFFSET, "offset" : 38 * mm, "width" : 150 * mm, "height" : 150 * mm});
        }
        {
            var Q0;
            Q0=qCreatedBy(id+"F34.planeOp",FACE);
            var sketch = newSketch(context, id + "F35", { "sketchPlane" : qUnion([Q0])});
            skLineSegment(sketch, "E119.0", {"start": v(-135, -75) * mm, "end": v(-135, -117) * mm});
            skLineSegment(sketch, "E120.0", {"start": v(-107, -117) * mm, "end": v(-135, -117) * mm});
            skLineSegment(sketch, "E121.0", {"start": v(-107, -75) * mm, "end": v(-135, -75) * mm});
            skLineSegment(sketch, "E122.0", {"start": v(-107, -75) * mm, "end": v(-107, -117) * mm});
            skLineSegment(sketch, "E123.0", {"start": v(-135, -163) * mm, "end": v(-135, -205) * mm});
            skLineSegment(sketch, "E124.0", {"start": v(-107, -163) * mm, "end": v(-135, -163) * mm});
            skLineSegment(sketch, "E125.0", {"start": v(-107, -163) * mm, "end": v(-107, -205) * mm});
            skLineSegment(sketch, "E126.0", {"start": v(-107, -205) * mm, "end": v(-135, -205) * mm});
            skSolve(sketch);
        }
        {
            var Q0;
            Q0=makeQuery(id+"F35.imprint","IMPRINT",FACE,{"disambiguationData":[TD([[makeQuery(id+"F35.imprint","IMPRINT",EDGE,{"derivedFrom":sQuery(id+"F35.wireOp",EDGE,"E123.0")}),1.0]])]});
            var Q1;
            Q1=makeQuery(id+"F35.imprint","IMPRINT",FACE,{"disambiguationData":[TD([[makeQuery(id+"F35.imprint","IMPRINT",EDGE,{"derivedFrom":sQuery(id+"F35.wireOp",EDGE,"E119.0")}),1.0]])]});
            extrude(context, id + "F36", {"entities" : qUnion([Q0, Q1]), "depth" : 36 * mm});
        }
    });
